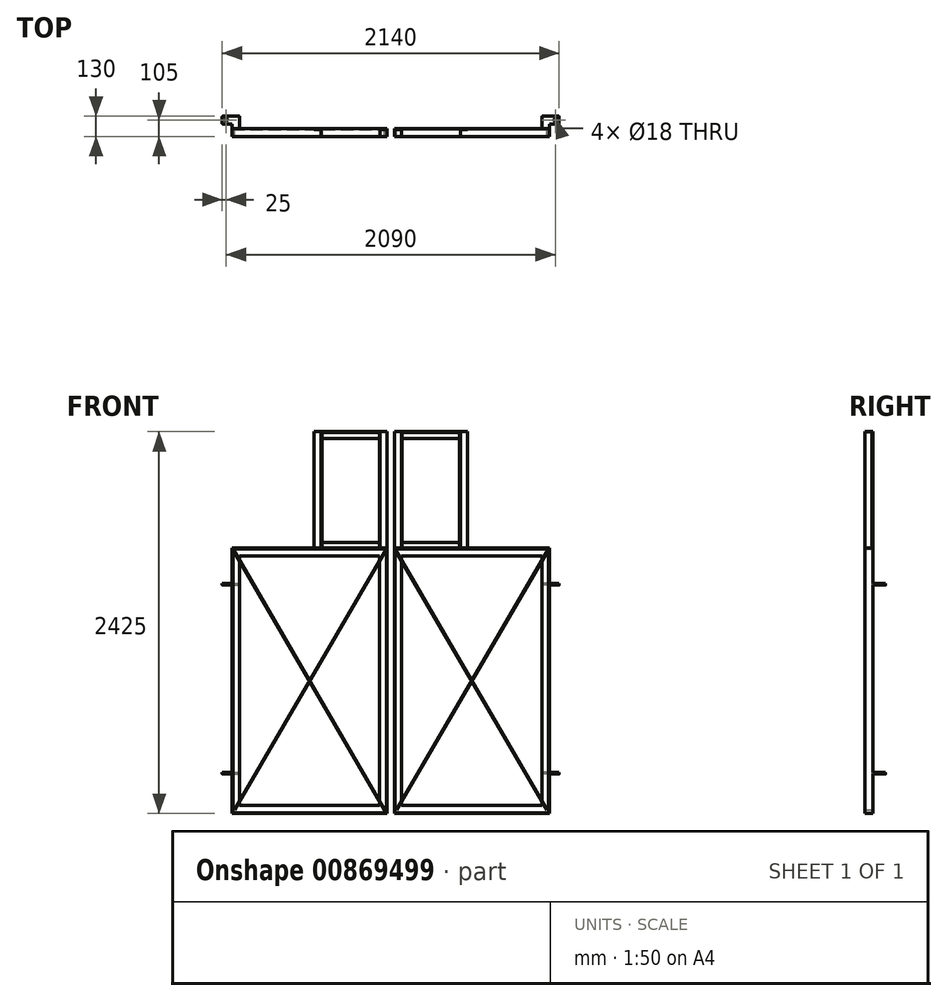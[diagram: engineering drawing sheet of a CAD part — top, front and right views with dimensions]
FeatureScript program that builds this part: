
annotation { "Feature Type Name" : "Feature", "Feature Type Description" : "" }
export const myFeature = defineFeature(function(context is Context, id is Id, definition is map)
    precondition{}
    {
        {
            var Q0;
            Q0=qCreatedBy(makeId("Front.planeOp"),FACE);
            var sketch = newSketch(context, id + "F0", { "sketchPlane" : qUnion([Q0])});
            skLineSegment(sketch, "E0.bottom", {"start": v(-492.5, 842.5) * mm, "end": v(492.5, 842.5) * mm});
            skLineSegment(sketch, "E0.top", {"start": v(-492.5, -842.5) * mm, "end": v(492.5, -842.5) * mm});
            skLineSegment(sketch, "E0.left", {"start": v(-492.5, 842.5) * mm, "end": v(-492.5, -842.5) * mm});
            skLineSegment(sketch, "E0.right", {"start": v(492.5, 842.5) * mm, "end": v(492.5, -842.5) * mm});
            skSolve(sketch);
        }
        {
            var Q0;
            Q0 = qSketchRegion(id + "F0", true);
            extrude(context, id + "F1", {"entities" : qUnion([Q0]), "depth" : 50 * mm, "offsetDistance" : 25 * mm});
        }
        {
            var Q0;
            Q0=makeQuery(id+"F1.opExtrude","CAP_FACE",FACE,{"disambiguationData":[OSD([sQuery(id+"F0.wireOp",EDGE,"E0.bottom"),sQuery(id+"F0.wireOp",EDGE,"E0.top"),sQuery(id+"F0.wireOp",EDGE,"E0.left"),sQuery(id+"F0.wireOp",EDGE,"E0.right")])],"isStart":false});
            shell(context, id + "F2", {"entities" : qUnion([Q0]), "thickness" : 5 * mm});
        }
        {
            var Q0;
            Q0=makeQuery(id+"F1.opExtrude","CAP_FACE",FACE,{"disambiguationData":[OSD([sQuery(id+"F0.wireOp",EDGE,"E0.bottom"),sQuery(id+"F0.wireOp",EDGE,"E0.top"),sQuery(id+"F0.wireOp",EDGE,"E0.left"),sQuery(id+"F0.wireOp",EDGE,"E0.right")])],"isStart":false});
            var sketch = newSketch(context, id + "F3", { "sketchPlane" : qUnion([Q0])});
            skLineSegment(sketch, "E1.bottom", {"start": v(445, 792.5) * mm, "end": v(-445, 792.5) * mm});
            skLineSegment(sketch, "E1.top", {"start": v(445, -792.5) * mm, "end": v(-445, -792.5) * mm});
            skLineSegment(sketch, "E1.left", {"start": v(445, 792.5) * mm, "end": v(445, -792.5) * mm});
            skLineSegment(sketch, "E1.right", {"start": v(-445, 792.5) * mm, "end": v(-445, -792.5) * mm});
            skPoint(sketch, "E1.middle", {"position": v(0, 0) * mm});
            skSolve(sketch);
        }
        {
            var Q0;
            Q0 = qSketchRegion(id + "F3", true);
            extrude(context, id + "F4", {"entities" : qUnion([Q0]), "operationType" : NewBodyOperationType.REMOVE, "endBound" : BoundingType.THROUGH_ALL, "oppositeDirection" : true, "depth" : 25 * mm, "offsetDistance" : 25 * mm});
        }
        {
            var Q0;
            Q0=qCreatedBy(makeId("Front.planeOp"),FACE);
            var sketch = newSketch(context, id + "F5", { "sketchPlane" : qUnion([Q0])});
            skLineSegment(sketch, "E2", {"start": v(0, 0) * mm, "end": v(0, 842.5) * mm, "construction": true});
            skLineSegment(sketch, "E3", {"start": v(0, 842.5) * mm, "end": v(447.5, 842.5) * mm, "construction": true});
            skLineSegment(sketch, "E4.bottom", {"start": v(447.5, 842.5) * mm, "end": v(72.5, 842.5) * mm});
            skLineSegment(sketch, "E4.top", {"start": v(447.5, 1582.5) * mm, "end": v(72.5, 1582.5) * mm});
            skLineSegment(sketch, "E4.left", {"start": v(447.5, 842.5) * mm, "end": v(447.5, 1582.5) * mm});
            skLineSegment(sketch, "E4.right", {"start": v(72.5, 842.5) * mm, "end": v(72.5, 1582.5) * mm});
            skSolve(sketch);
        }
        {
            var Q0;
            Q0 = qSketchRegion(id + "F5", true);
            extrude(context, id + "F6", {"entities" : qUnion([Q0]), "operationType" : NewBodyOperationType.ADD, "depth" : 50 * mm, "offsetDistance" : 25 * mm});
        }
        {
            var Q0;
            Q0=makeQuery(id+"F6.boolean.opBoolean","MERGE",FACE,{"derivedFrom":[makeQuery(id+"F1.opExtrude","CAP_FACE",FACE,{"disambiguationData":[OSD([sQuery(id+"F0.wireOp",EDGE,"E0.bottom"),sQuery(id+"F0.wireOp",EDGE,"E0.top"),sQuery(id+"F0.wireOp",EDGE,"E0.left"),sQuery(id+"F0.wireOp",EDGE,"E0.right")])],"isStart":false}),makeQuery(id+"F6.opExtrude","CAP_FACE",FACE,{"disambiguationData":[OSD([sQuery(id+"F5.wireOp",EDGE,"fHkwlImH-BFT2-xzur-VwpF-hZ0MvCgmQI08.bottom"),sQuery(id+"F5.wireOp",EDGE,"fHkwlImH-BFT2-xzur-VwpF-hZ0MvCgmQI08.top"),sQuery(id+"F5.wireOp",EDGE,"fHkwlImH-BFT2-xzur-VwpF-hZ0MvCgmQI08.left"),sQuery(id+"F5.wireOp",EDGE,"fHkwlImH-BFT2-xzur-VwpF-hZ0MvCgmQI08.right")])],"isStart":false})]});
            shell(context, id + "F7", {"entities" : qUnion([Q0]), "thickness" : 5 * mm});
        }
        {
            var Q0;
            Q0=makeQuery(id+"F7.opShell","OFFSET_FACE",FACE,{"disambiguationData":[OSD([sQuery(id+"F0.wireOp",EDGE,"E0.bottom"),sQuery(id+"F0.wireOp",EDGE,"E0.top"),sQuery(id+"F0.wireOp",EDGE,"E0.left"),sQuery(id+"F0.wireOp",EDGE,"E0.right"),sQuery(id+"F5.wireOp",EDGE,"E4.bottom"),sQuery(id+"F5.wireOp",EDGE,"E4.top"),sQuery(id+"F5.wireOp",EDGE,"E4.left"),sQuery(id+"F5.wireOp",EDGE,"E4.right")])]});
            var sketch = newSketch(context, id + "F8", { "sketchPlane" : qUnion([Q0])});
            skLineSegment(sketch, "E5", {"start": v(77.5, 1210) * mm, "end": v(260, 1210) * mm, "construction": true});
            skPoint(sketch, "E5.endSnap0", {"position": v(260, 1577.5) * mm});
            skLineSegment(sketch, "E6.bottom", {"start": v(442.5, 1540) * mm, "end": v(77.5, 1540) * mm});
            skLineSegment(sketch, "E6.top", {"start": v(442.5, 880) * mm, "end": v(77.5, 880) * mm});
            skLineSegment(sketch, "E6.left", {"start": v(442.5, 1540) * mm, "end": v(442.5, 880) * mm});
            skLineSegment(sketch, "E6.right", {"start": v(77.5, 1540) * mm, "end": v(77.5, 880) * mm});
            skPoint(sketch, "E6.middle", {"position": v(260, 1210) * mm});
            skSolve(sketch);
        }
        {
            var Q0;
            Q0 = qSketchRegion(id + "F8", true);
            extrude(context, id + "F9", {"entities" : qUnion([Q0]), "operationType" : NewBodyOperationType.REMOVE, "endBound" : BoundingType.THROUGH_ALL, "oppositeDirection" : true, "depth" : 25 * mm, "offsetDistance" : 25 * mm});
        }
        {
            var Q0;
            {var subQ4=sQuery(id+"F0.wireOp",EDGE,"E0.left");var subQ7=sQuery(id+"F0.wireOp",EDGE,"E0.bottom");Q0=makeQuery(id+"F6.boolean.opBoolean","SPLIT",FACE,{"disambiguationData":[TD([makeQuery(id+"F1.opExtrude","SWEPT_FACE",FACE,{"disambiguationData":[OSD([subQ4])]})])],"derivedFrom":makeQuery(id+"F1.opExtrude","SWEPT_FACE",FACE,{"disambiguationData":[OSD([subQ7])]})});}
            var sketch = newSketch(context, id + "F10", { "sketchPlane" : qUnion([Q0])});
            skLineSegment(sketch, "E7.bottom", {"start": v(72.5, 0) * mm, "end": v(27.5, 0) * mm});
            skLineSegment(sketch, "E7.top", {"start": v(72.5, -5) * mm, "end": v(27.5, -5) * mm});
            skLineSegment(sketch, "E7.left", {"start": v(72.5, 0) * mm, "end": v(72.5, -5) * mm});
            skLineSegment(sketch, "E7.right", {"start": v(27.5, 0) * mm, "end": v(27.5, -5) * mm});
            skLineSegment(sketch, "E8", {"start": v(72.5, 0) * mm, "end": v(260, 0) * mm, "construction": true});
            skLineSegment(sketch, "E9", {"start": v(260, 0) * mm, "end": v(260, -43.7) * mm, "construction": true});
            skLineSegment(sketch, "E10.MirrorCS", {"start": v(447.5, 0) * mm, "end": v(447.5, -5) * mm});
            skLineSegment(sketch, "E11.MirrorCS", {"start": v(492.5, 0) * mm, "end": v(492.5, -5) * mm});
            skLineSegment(sketch, "E12.MirrorCS", {"start": v(447.5, -5) * mm, "end": v(492.5, -5) * mm});
            skLineSegment(sketch, "E13.MirrorCS", {"start": v(447.5, 0) * mm, "end": v(492.5, 0) * mm});
            skSolve(sketch);
        }
        {
            var Q0;
            Q0 = qSketchRegion(id + "F10", true);
            extrude(context, id + "F11", {"entities" : qUnion([Q0]), "operationType" : NewBodyOperationType.ADD, "depth" : 740 * mm, "offsetDistance" : 25 * mm});
        }
        {
            var Q0;
            Q0=makeQuery(id+"F2.opShell","OFFSET_FACE",FACE,{"disambiguationData":[OSD([sQuery(id+"F0.wireOp",EDGE,"E0.bottom"),sQuery(id+"F0.wireOp",EDGE,"E0.top"),sQuery(id+"F0.wireOp",EDGE,"E0.left"),sQuery(id+"F0.wireOp",EDGE,"E0.right")])]});
            var sketch = newSketch(context, id + "F12", { "sketchPlane" : qUnion([Q0])});
            skLineSegment(sketch, "E14.0", {"start": v(-487.5, 836.24) * mm, "end": v(487.86, -837.5) * mm});
            skLineSegment(sketch, "E15.0", {"start": v(-489.58, 837.5) * mm, "end": v(487.5, -836.86) * mm});
            skLineSegment(sketch, "E16", {"start": v(487.5, -837.5) * mm, "end": v(487.86, -837.5) * mm});
            skLineSegment(sketch, "E17", {"start": v(487.5, -837.5) * mm, "end": v(487.5, -836.86) * mm});
            skLineSegment(sketch, "E18", {"start": v(-487.5, 836.24) * mm, "end": v(-487.5, 837.5) * mm});
            skLineSegment(sketch, "E19", {"start": v(-489.58, 837.5) * mm, "end": v(-487.5, 837.5) * mm});
            skSolve(sketch);
        }
        {
            var Q0;
            Q0 = qSketchRegion(id + "F12", true);
            extrude(context, id + "F13", {"entities" : qUnion([Q0]), "depth" : 45 * mm, "offsetDistance" : 25 * mm});
        }
        {
            var Q0;
            Q0=makeQuery(id+"F13.opExtrude","SWEPT_BODY",BODY,{"disambiguationData":[OSD([sQuery(id+"F12.wireOp",EDGE,"E14.0"),sQuery(id+"F12.wireOp",EDGE,"E15.0"),sQuery(id+"F12.wireOp",EDGE,"E16"),sQuery(id+"F12.wireOp",EDGE,"E17"),sQuery(id+"F12.wireOp",EDGE,"E18"),sQuery(id+"F12.wireOp",EDGE,"E19")])]});
            var Q1;
            Q1=qCreatedBy(makeId("Right.planeOp"),FACE);
            mirror(context, id + "F14", {"entities" : qUnion([Q0]), "mirrorPlane" : qUnion([Q1])});
        }
        {
            var Q0;
            Q0=qCreatedBy(makeId("Right.planeOp"),FACE);
            cPlane(context, id + "F15", {"entities" : qUnion([Q0]), "cplaneType" : CPlaneType.OFFSET, "offset" : 515 * mm, "width" : 150 * mm, "height" : 150 * mm});
        }
        {
            var Q0;
            Q0=makeQuery(id+"F11.boolean.opBoolean","MERGE",FACE,{"derivedFrom":[makeQuery(id+"F6.boolean.opBoolean","MERGE",FACE,{"derivedFrom":[makeQuery(id+"F1.opExtrude","CAP_FACE",FACE,{"disambiguationData":[OSD([sQuery(id+"F0.wireOp",EDGE,"E0.bottom"),sQuery(id+"F0.wireOp",EDGE,"E0.top"),sQuery(id+"F0.wireOp",EDGE,"E0.left"),sQuery(id+"F0.wireOp",EDGE,"E0.right")])],"isStart":true}),makeQuery(id+"F6.opExtrude","CAP_FACE",FACE,{"disambiguationData":[OSD([sQuery(id+"F5.wireOp",EDGE,"E4.bottom"),sQuery(id+"F5.wireOp",EDGE,"E4.top"),sQuery(id+"F5.wireOp",EDGE,"E4.left"),sQuery(id+"F5.wireOp",EDGE,"E4.right")])],"isStart":true})]}),makeQuery(id+"F11.opExtrude","SWEPT_FACE",FACE,{"disambiguationData":[OSD([sQuery(id+"F10.wireOp",EDGE,"E7.bottom")])]}),makeQuery(id+"F11.opExtrude","SWEPT_FACE",FACE,{"disambiguationData":[OSD([sQuery(id+"F10.wireOp",EDGE,"E13.MirrorCS")])]})]});
            var sketch = newSketch(context, id + "F16", { "sketchPlane" : qUnion([Q0])});
            skLineSegment(sketch, "E20", {"start": v(492.5, -842.5) * mm, "end": v(492.5, -592.5) * mm, "construction": true});
            skLineSegment(sketch, "E21.bottom", {"start": v(492.5, -592.5) * mm, "end": v(445, -592.5) * mm});
            skLineSegment(sketch, "E21.top", {"start": v(492.5, -582.5) * mm, "end": v(445, -582.5) * mm});
            skLineSegment(sketch, "E21.left", {"start": v(492.5, -592.5) * mm, "end": v(492.5, -582.5) * mm});
            skLineSegment(sketch, "E21.right", {"start": v(445, -592.5) * mm, "end": v(445, -582.5) * mm});
            skLineSegment(sketch, "E22", {"start": v(492.5, 842.5) * mm, "end": v(492.5, 617.5) * mm, "construction": true});
            skLineSegment(sketch, "E23.bottom", {"start": v(492.5, 617.5) * mm, "end": v(445, 617.5) * mm});
            skLineSegment(sketch, "E23.top", {"start": v(492.5, 607.5) * mm, "end": v(445, 607.5) * mm});
            skLineSegment(sketch, "E23.left", {"start": v(492.5, 617.5) * mm, "end": v(492.5, 607.5) * mm});
            skLineSegment(sketch, "E23.right", {"start": v(445, 617.5) * mm, "end": v(445, 607.5) * mm});
            skSolve(sketch);
        }
        {
            var Q0;
            Q0 = qSketchRegion(id + "F16", true);
            extrude(context, id + "F17", {"entities" : qUnion([Q0]), "operationType" : NewBodyOperationType.ADD, "depth" : 80 * mm, "offsetDistance" : 25 * mm});
        }
        {
            var Q0;
            Q0=makeQuery(id+"F17.boolean.opBoolean","MERGE",FACE,{"derivedFrom":[makeQuery(id+"F1.opExtrude","SWEPT_FACE",FACE,{"disambiguationData":[OSD([sQuery(id+"F0.wireOp",EDGE,"E0.left")])]}),makeQuery(id+"F17.opExtrude","SWEPT_FACE",FACE,{"disambiguationData":[OSD([sQuery(id+"F16.wireOp",EDGE,"E21.left")])]}),makeQuery(id+"F17.opExtrude","SWEPT_FACE",FACE,{"disambiguationData":[OSD([sQuery(id+"F16.wireOp",EDGE,"E23.left")])]})]});
            var sketch = newSketch(context, id + "F18", { "sketchPlane" : qUnion([Q0])});
            skLineSegment(sketch, "E24.bottom", {"start": v(-80, 617.5) * mm, "end": v(-30, 617.5) * mm});
            skLineSegment(sketch, "E24.top", {"start": v(-80, 607.5) * mm, "end": v(-30, 607.5) * mm});
            skLineSegment(sketch, "E24.left", {"start": v(-80, 617.5) * mm, "end": v(-80, 607.5) * mm});
            skLineSegment(sketch, "E24.right", {"start": v(-30, 617.5) * mm, "end": v(-30, 607.5) * mm});
            skLineSegment(sketch, "E25.bottom", {"start": v(-80, -582.5) * mm, "end": v(-30, -582.5) * mm});
            skLineSegment(sketch, "E25.top", {"start": v(-80, -592.5) * mm, "end": v(-30, -592.5) * mm});
            skLineSegment(sketch, "E25.left", {"start": v(-80, -582.5) * mm, "end": v(-80, -592.5) * mm});
            skLineSegment(sketch, "E25.right", {"start": v(-30, -582.5) * mm, "end": v(-30, -592.5) * mm});
            skSolve(sketch);
        }
        {
            var Q0;
            Q0 = qSketchRegion(id + "F18", true);
            extrude(context, id + "F19", {"entities" : qUnion([Q0]), "operationType" : NewBodyOperationType.ADD, "depth" : 62.5 * mm, "offsetDistance" : 25 * mm});
        }
        {
            var Q0;
            Q0=makeQuery(id+"F19.boolean.opBoolean","MERGE",FACE,{"derivedFrom":[makeQuery(id+"F17.opExtrude","SWEPT_FACE",FACE,{"disambiguationData":[OSD([sQuery(id+"F16.wireOp",EDGE,"E23.bottom")])]}),makeQuery(id+"F19.opExtrude","SWEPT_FACE",FACE,{"disambiguationData":[OSD([sQuery(id+"F18.wireOp",EDGE,"E24.bottom")])]})]});
            var sketch = newSketch(context, id + "F20", { "sketchPlane" : qUnion([Q0])});
            skCircle(sketch, "E26", {"center": v(-530, 55) * mm, "radius": 9 * mm});
            skPoint(sketch, "E26.centerSnap0", {"position": v(-555, 55) * mm});
            skSolve(sketch);
        }
        {
            var Q0;
            Q0 = qSketchRegion(id + "F20", true);
            extrude(context, id + "F21", {"entities" : qUnion([Q0]), "operationType" : NewBodyOperationType.REMOVE, "endBound" : BoundingType.THROUGH_ALL, "oppositeDirection" : true, "depth" : 25 * mm, "offsetDistance" : 25 * mm});
        }
        {
            var Q0;
            Q0=makeQuery(id+"F17.opExtrude","CAP_EDGE",EDGE,{"disambiguationData":[OSD([sQuery(id+"F16.wireOp",EDGE,"E23.right")])],"isStart":false});
            var Q1;
            Q1=makeQuery(id+"F19.opExtrude","CAP_EDGE",EDGE,{"disambiguationData":[OSD([sQuery(id+"F18.wireOp",EDGE,"E24.left")])],"isStart":false});
            var Q2;
            Q2=makeQuery(id+"F19.opExtrude","CAP_EDGE",EDGE,{"disambiguationData":[OSD([sQuery(id+"F18.wireOp",EDGE,"E24.right")])],"isStart":false});
            var Q3;
            Q3=makeQuery(id+"F19.opExtrude","CAP_EDGE",EDGE,{"disambiguationData":[OSD([sQuery(id+"F18.wireOp",EDGE,"E25.right")])],"isStart":false});
            var Q4;
            Q4=makeQuery(id+"F19.opExtrude","CAP_EDGE",EDGE,{"disambiguationData":[OSD([sQuery(id+"F18.wireOp",EDGE,"E25.left")])],"isStart":false});
            var Q5;
            Q5=makeQuery(id+"F17.opExtrude","CAP_EDGE",EDGE,{"disambiguationData":[OSD([sQuery(id+"F16.wireOp",EDGE,"E21.right")])],"isStart":false});
            fillet(context, id + "F22", {"entities" : qUnion([Q0, Q1, Q2, Q3, Q4, Q5]), "radius" : 5 * mm, "tangentPropagation" : true, "allowEdgeOverflow" : false});
        }
        {
            var Q0;
            Q0=makeQuery(id+"F1.opExtrude","SWEPT_BODY",BODY,{"disambiguationData":[OSD([sQuery(id+"F0.wireOp",EDGE,"E0.bottom"),sQuery(id+"F0.wireOp",EDGE,"E0.top"),sQuery(id+"F0.wireOp",EDGE,"E0.left"),sQuery(id+"F0.wireOp",EDGE,"E0.right")])]});
            var Q1;
            Q1=makeQuery(id+"F13.opExtrude","SWEPT_BODY",BODY,{"disambiguationData":[OSD([sQuery(id+"F12.wireOp",EDGE,"E14.0"),sQuery(id+"F12.wireOp",EDGE,"E15.0"),sQuery(id+"F12.wireOp",EDGE,"E16"),sQuery(id+"F12.wireOp",EDGE,"E17"),sQuery(id+"F12.wireOp",EDGE,"E18"),sQuery(id+"F12.wireOp",EDGE,"E19")])]});
            var Q2;
            Q2=makeQuery(id+"F14.opPattern","COPY",BODY,{"derivedFrom":makeQuery(id+"F13.opExtrude","SWEPT_BODY",BODY,{"disambiguationData":[OSD([sQuery(id+"F12.wireOp",EDGE,"E14.0"),sQuery(id+"F12.wireOp",EDGE,"E15.0"),sQuery(id+"F12.wireOp",EDGE,"E16"),sQuery(id+"F12.wireOp",EDGE,"E17"),sQuery(id+"F12.wireOp",EDGE,"E18"),sQuery(id+"F12.wireOp",EDGE,"E19")])]}),"instanceName":"1"});
            var Q3;
            Q3=qCreatedBy(id+"F15.planeOp",FACE);
            mirror(context, id + "F23", {"entities" : qUnion([Q0, Q1, Q2]), "mirrorPlane" : qUnion([Q3])});
        }
    });
